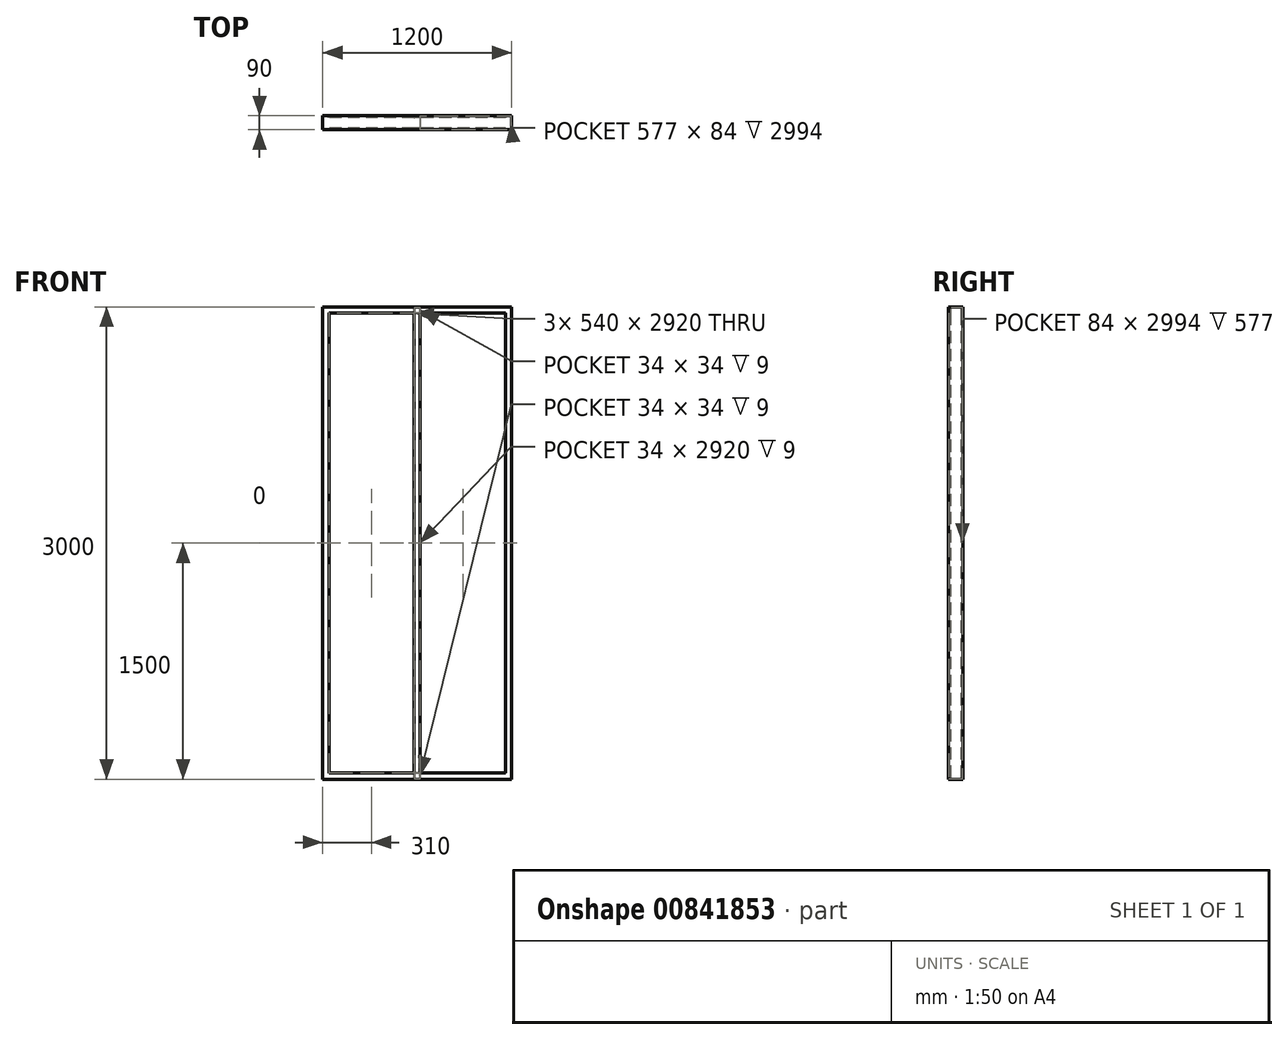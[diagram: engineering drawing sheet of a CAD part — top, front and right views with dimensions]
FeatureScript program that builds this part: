
annotation { "Feature Type Name" : "Feature", "Feature Type Description" : "" }
export const myFeature = defineFeature(function(context is Context, id is Id, definition is map)
    precondition{}
    {
        {
            var Q0;
            Q0=qCreatedBy(makeId("Front.planeOp"),FACE);
            var sketch = newSketch(context, id + "F0", { "sketchPlane" : qUnion([Q0])});
            skLineSegment(sketch, "E0.bottom", {"start": v(0, 0) * mm, "end": v(1200, 0) * mm});
            skLineSegment(sketch, "E0.top", {"start": v(0, 3000) * mm, "end": v(1200, 3000) * mm});
            skLineSegment(sketch, "E0.left", {"start": v(0, 0) * mm, "end": v(0, 3000) * mm});
            skLineSegment(sketch, "E0.right", {"start": v(1200, 0) * mm, "end": v(1200, 3000) * mm});
            skSolve(sketch);
        }
        {
            var Q0;
            Q0=qCreatedBy(makeId("Top.planeOp"),FACE);
            var sketch = newSketch(context, id + "F1", { "sketchPlane" : qUnion([Q0])});
            skLineSegment(sketch, "E1", {"start": v(0, 0) * mm, "end": v(0, -45) * mm});
            skLineSegment(sketch, "E2", {"start": v(0, -45) * mm, "end": v(40, -45) * mm});
            skLineSegment(sketch, "E3", {"start": v(40, -45) * mm, "end": v(40, -33) * mm});
            skLineSegment(sketch, "E4.MirrorCS", {"start": v(0, 0) * mm, "end": v(0, 45) * mm});
            skLineSegment(sketch, "E5.MirrorCS", {"start": v(0, 45) * mm, "end": v(40, 45) * mm});
            skLineSegment(sketch, "E6.MirrorCS", {"start": v(40, 45) * mm, "end": v(40, 33) * mm});
            skLineSegment(sketch, "E7.0", {"start": v(37, 42) * mm, "end": v(37, 33) * mm});
            skLineSegment(sketch, "E7.1", {"start": v(3, 42) * mm, "end": v(37, 42) * mm});
            skLineSegment(sketch, "E7.2", {"start": v(37, -42) * mm, "end": v(37, -33) * mm});
            skLineSegment(sketch, "E7.3", {"start": v(3, -42) * mm, "end": v(37, -42) * mm});
            skLineSegment(sketch, "E7.4", {"start": v(3, 0) * mm, "end": v(3, -42) * mm});
            skLineSegment(sketch, "E7.5", {"start": v(3, 0) * mm, "end": v(3, 42) * mm});
            skLineSegment(sketch, "E8", {"start": v(37, 33) * mm, "end": v(40, 33) * mm});
            skLineSegment(sketch, "E9", {"start": v(37, -33) * mm, "end": v(40, -33) * mm});
            skSolve(sketch);
        }
        {
            var Q0;
            Q0=qSketchRegion(id+"F1",true);
            var Q1;
            Q1=qConstructionFilter(qBodyType(qCreatedBy(id+"F0",EDGE),BodyType.WIRE),ConstructionObject.NO);
            sweep(context, id + "F2", {"profiles" : qUnion([Q0]), "path" : qUnion([Q1])});
        }
        {
            var Q0;
            Q0=qCreatedBy(makeId("Top.planeOp"),FACE);
            var sketch = newSketch(context, id + "F3", { "sketchPlane" : qUnion([Q0])});
            skLineSegment(sketch, "E10", {"start": v(580, -45) * mm, "end": v(620, -45) * mm});
            skLineSegment(sketch, "E11", {"start": v(620, -45) * mm, "end": v(620, 45) * mm});
            skLineSegment(sketch, "E12", {"start": v(620, 45) * mm, "end": v(580, 45) * mm});
            skLineSegment(sketch, "E13", {"start": v(580, 45) * mm, "end": v(580, 33) * mm});
            skLineSegment(sketch, "E14", {"start": v(580, -45) * mm, "end": v(580, -33) * mm});
            skLineSegment(sketch, "E15", {"start": v(900, -276.13) * mm, "end": v(900, 155.47) * mm, "construction": true});
            skLineSegment(sketch, "E16.0", {"start": v(1195, -40) * mm, "end": v(5, -40) * mm});
            skLineSegment(sketch, "E16.1", {"start": v(1195, 40) * mm, "end": v(1195, -40) * mm});
            skLineSegment(sketch, "E16.2", {"start": v(5, 40) * mm, "end": v(1195, 40) * mm});
            skLineSegment(sketch, "E16.3", {"start": v(5, 40) * mm, "end": v(5, -40) * mm});
            skLineSegment(sketch, "E17.0", {"start": v(583, 42) * mm, "end": v(583, 33) * mm});
            skLineSegment(sketch, "E17.1", {"start": v(583, -42) * mm, "end": v(583, -33) * mm});
            skLineSegment(sketch, "E17.2", {"start": v(583, -42) * mm, "end": v(617, -42) * mm});
            skLineSegment(sketch, "E17.3", {"start": v(617, -42) * mm, "end": v(617, 42) * mm});
            skLineSegment(sketch, "E17.4", {"start": v(617, 42) * mm, "end": v(583, 42) * mm});
            skLineSegment(sketch, "E18", {"start": v(583, -33) * mm, "end": v(580, -33) * mm});
            skLineSegment(sketch, "E19", {"start": v(583, 33) * mm, "end": v(580, 33) * mm});
            skSolve(sketch);
        }
        {
            var Q0;
            {var subQ1=sQuery(id+"F3.wireOp",EDGE,"E10");Q0=makeQuery(id+"F3.imprint","IMPRINT",FACE,{"disambiguationData":[TD([[makeQuery(id+"F3.imprint","IMPRINT",EDGE,{"derivedFrom":subQ1}),1.0]])]});}
            var Q1;
            {var subQ0=sQuery(id+"F3.wireOp",EDGE,"E16.0");var subQ1=sQuery(id+"F3.wireOp",EDGE,"E11");var subQ2=makeQuery(id+"F3.imprint","INTERSECT",VERTEX,{"derivedFrom":[subQ1,subQ0]});Q1=makeQuery(id+"F3.imprint","IMPRINT",FACE,{"disambiguationData":[TD([[makeQuery(id+"F3.imprint","IMPRINT",EDGE,{"disambiguationData":[TD([[subQ2,-1.0]])],"derivedFrom":subQ1}),1.0]])]});}
            var Q2;
            {var subQ0=sQuery(id+"F3.wireOp",EDGE,"E18");Q2=makeQuery(id+"F3.imprint","IMPRINT",FACE,{"disambiguationData":[TD([[makeQuery(id+"F3.imprint","IMPRINT",EDGE,{"derivedFrom":subQ0}),1.0]])]});}
            var Q3;
            {var subQ1=sQuery(id+"F3.wireOp",EDGE,"E12");Q3=makeQuery(id+"F3.imprint","IMPRINT",FACE,{"disambiguationData":[TD([[makeQuery(id+"F3.imprint","IMPRINT",EDGE,{"derivedFrom":subQ1}),1.0]])]});}
            var Q4;
            {var subQ0=sQuery(id+"F3.wireOp",EDGE,"E19");Q4=makeQuery(id+"F3.imprint","IMPRINT",FACE,{"disambiguationData":[TD([[makeQuery(id+"F3.imprint","IMPRINT",EDGE,{"derivedFrom":subQ0}),-1.0]])]});}
            var Q5;
            {var subQ0=sQuery(id+"F3.wireOp",EDGE,"fbeb7f0c-a459-400f-91ed-7fec257c8f050.MirrorCS");Q5=makeQuery(id+"F3.imprint","IMPRINT",FACE,{"disambiguationData":[TD([[makeQuery(id+"F3.imprint","IMPRINT",EDGE,{"derivedFrom":subQ0}),1.0]])]});}
            var Q6;
            {var subQ1=sQuery(id+"F3.wireOp",EDGE,"567eaf2c-da89-443f-b3b3-d68592a5250c0.MirrorCS");Q6=makeQuery(id+"F3.imprint","IMPRINT",FACE,{"disambiguationData":[TD([[makeQuery(id+"F3.imprint","IMPRINT",EDGE,{"derivedFrom":subQ1}),-1.0]])]});}
            var Q7;
            {var subQ0=sQuery(id+"F3.wireOp",EDGE,"E16.0");var subQ1=sQuery(id+"F3.wireOp",EDGE,"1e470031-5891-413e-a47c-f06d65b3e17f0.MirrorCS");var subQ2=makeQuery(id+"F3.imprint","INTERSECT",VERTEX,{"derivedFrom":[subQ1,subQ0]});Q7=makeQuery(id+"F3.imprint","IMPRINT",FACE,{"disambiguationData":[TD([[makeQuery(id+"F3.imprint","IMPRINT",EDGE,{"disambiguationData":[TD([[subQ2,-1.0]])],"derivedFrom":subQ1}),-1.0]])]});}
            var Q8;
            {var subQ5=sQuery(id+"F3.wireOp",EDGE,"ca9fbca5-8cf1-4a5b-8b27-837bc25230130.MirrorCS");Q8=makeQuery(id+"F3.imprint","IMPRINT",FACE,{"disambiguationData":[TD([[makeQuery(id+"F3.imprint","IMPRINT",EDGE,{"derivedFrom":subQ5}),-1.0]])]});}
            var Q9;
            {var subQ0=sQuery(id+"F3.wireOp",EDGE,"47aaed49-ff0d-4512-a623-d8c6419a6b470.MirrorCS");Q9=makeQuery(id+"F3.imprint","IMPRINT",FACE,{"disambiguationData":[TD([[makeQuery(id+"F3.imprint","IMPRINT",EDGE,{"derivedFrom":subQ0}),-1.0]])]});}
            var Q10;
            Q10=makeQuery(id+"F2.opSweep","SWEPT_FACE",FACE,{"disambiguationData":[OSD([sQuery(id+"F0.wireOp",EDGE,"E0.top"),sQuery(id+"F1.wireOp",EDGE,"E7.4"),sQuery(id+"F1.wireOp",EDGE,"E7.5")])]});
            extrude(context, id + "F4", {"entities" : qUnion([Q0, Q1, Q2, Q3, Q4, Q5, Q6, Q7, Q8, Q9]), "operationType" : NewBodyOperationType.ADD, "endBound" : BoundingType.UP_TO_SURFACE, "depth" : 25 * mm, "endBoundEntityFace" : qUnion([Q10]), "offsetDistance" : 25 * mm});
        }
    });
